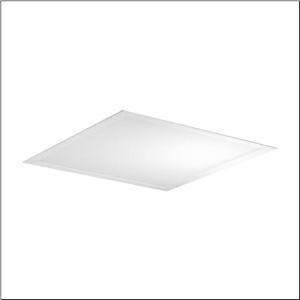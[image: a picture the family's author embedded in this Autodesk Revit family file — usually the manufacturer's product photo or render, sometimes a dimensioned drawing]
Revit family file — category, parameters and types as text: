
# Revit family: apollon_r__21_square_51mq11w72414_6b47
name_source: partatom
category: Lighting Fixtures
units: mm (PartAtom-declared; Revit-internal decimal feet)

## family parameters
Cut with Voids When Loaded = No
Host = Face
Light Source = No
Part Type = Normal
Room Calculation Point = No
Round Connector Dimension = Use Diameter
Shared = No

## types (1)
- Apollon® 21 square (1 x LED, 4200 lm, 23.3 W, 4000K)
    Apparent Load = 23 VA
    CIE Flux Codes = 60 87 97 100 100
    Color Rendering = 80
    Color Temperature = 4000K
    Default Elevation = 1800 mm
    Description = Apollon® 21 square, office luminaire, primary optical cover: micro prismatic cover, of PMMA, CAT 2 (L<= 3000cd/m²), light emission: direct distribution, primary light characteristic: symmetric, installation type: lay-in mounting, LED, rated luminous flux: 4.200lm, luminous efficacy: 180lm/W, light colour: 840, colour temperature: 4000K, with terminal, 3-pole, mains connection: 220..240V, AC/DC, 0/50..60Hz, rated input power: 23.3W, housing, of aluminium, coated, traffic white (RAL 9016), module: M625, length: 620mm, width: 620mm, height: 30mm, housing upper side, of sheet steel, galvanised, protection rating (complete): IP20, protection rating (lamp compartment, on room side): IP50, insulation class (complete): insulation class II (safety insulation), certification: CE, ENEC, impact resistance: IK03, permissible operating ambient temperature: -20..+45°C, permissible storage temperature: -40..+80°C, packaging unit: 1 piece
    Height = 0 mm  [stored 0 ft]
    Lamp = 1 x LED
    Lamp Light Flux = 4200 lm
    Lamp Power = 23.3 W
    Lamp count = 1
    Length = 620 mm
    Luminous efficacy = 180 lm/W
    Manufacturer = Siteco
    ModVariant = No
    Model = 51MQ11W72414
    Mounting Place = Ceiling
    Mounting Type = Recessed
    Number of Poles = 1
    OnlyDefault = Yes
    Power Factor = 1
    Product Name = Apollon® 21 square
    Product group = office luminaire | ceiling recessed
    ProductGroupID = 400
    Protection Class = Protection class II
    Protection Degree = IP 20
    RLX_Detail_Level = 1
    RLX_Emergency_Light_Flux = 0 lm
    RLX_Emergency_Type = 0
    RLX_Emergency_Type_DB = No
    RlxData = <blob elided: 12941 chars, md5=ff956628>
    Socket = socket
    Standby Power = 0 W
    System Light Flux = 4200 lm
    System Power = 23 W
    Type Comments = Product without accessories
    Type Image = l_1291054.jpg
    URL = http://relux.com
    VarID = ---
    Voltage = 0 V
    Weight = 0.00 kg
    Width = 620 mm

note: [stored X ft] marks values corroborated as IEEE doubles in the binary element streams (Revit-internal decimal feet)

## geometry (parser evidence)
native form markers: Sweep x9
no freeform markers — native parametric forms only
